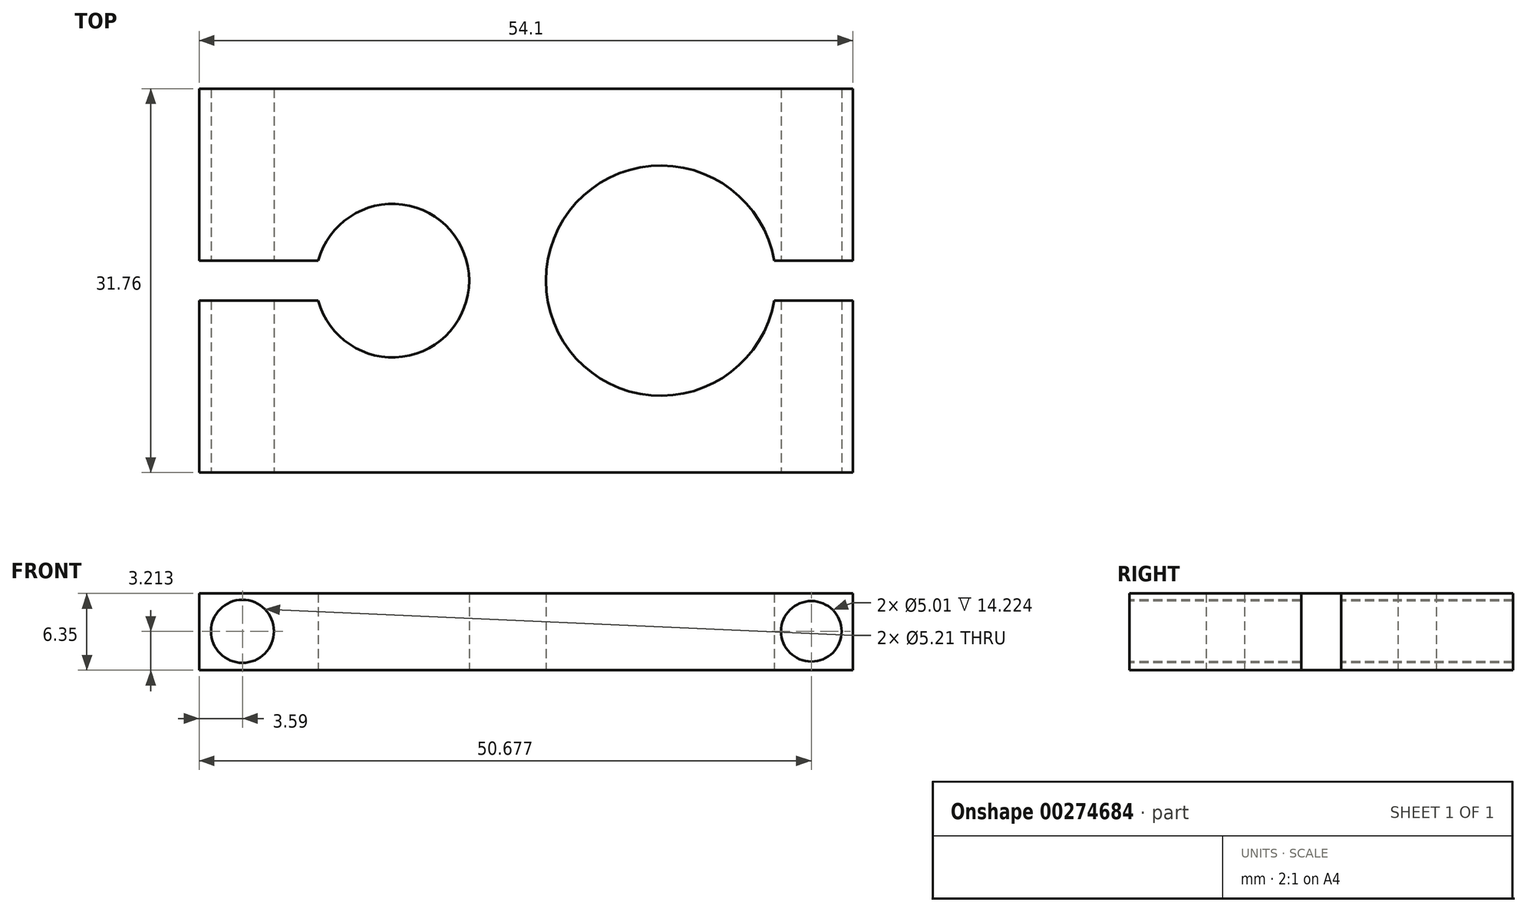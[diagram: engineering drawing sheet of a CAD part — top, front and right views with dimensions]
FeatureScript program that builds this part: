
annotation { "Feature Type Name" : "Feature", "Feature Type Description" : "" }
export const myFeature = defineFeature(function(context is Context, id is Id, definition is map)
    precondition{}
    {
        {
            var Q0;
            Q0=qCreatedBy(makeId("Top.planeOp"),FACE);
            var sketch = newSketch(context, id + "F0", { "sketchPlane" : qUnion([Q0])});
            skLineSegment(sketch, "E0.bottom", {"start": v(-27.05, 15.88) * mm, "end": v(27.05, 15.88) * mm});
            skLineSegment(sketch, "E0.top", {"start": v(-27.05, -15.88) * mm, "end": v(27.05, -15.88) * mm});
            skLineSegment(sketch, "E0.left", {"start": v(-27.05, 15.88) * mm, "end": v(-27.05, 1.65) * mm});
            skLineSegment(sketch, "E0.right", {"start": v(27.05, 15.88) * mm, "end": v(27.05, 1.65) * mm});
            skArc(sketch, "E1", {"start": v(20.56, 1.65) * mm, "mid": v(1.65, 0) * mm, "end": v(20.56, -1.65) * mm});
            skArc(sketch, "E2", {"start": v(-17.18, -1.65) * mm, "mid": v(-4.7, 0) * mm, "end": v(-17.18, 1.65) * mm});
            skLineSegment(sketch, "E3", {"start": v(-27.05, -1.65) * mm, "end": v(-17.18, -1.65) * mm});
            skLineSegment(sketch, "E4", {"start": v(-27.05, 1.65) * mm, "end": v(-17.18, 1.65) * mm});
            skLineSegment(sketch, "E5", {"start": v(20.56, 1.65) * mm, "end": v(27.05, 1.65) * mm});
            skLineSegment(sketch, "E6", {"start": v(27.05, -1.65) * mm, "end": v(20.56, -1.65) * mm});
            skLineSegment(sketch, "E7.trimOffspring", {"start": v(-27.05, -1.65) * mm, "end": v(-27.05, -15.88) * mm});
            skLineSegment(sketch, "E8.trimOffspring", {"start": v(27.05, -1.65) * mm, "end": v(27.05, -15.88) * mm});
            skSolve(sketch);
        }
        {
            var Q0;
            Q0 = qSketchRegion(id + "F0", true);
            var Q1;
            Q1=sQuery(id+"F0.wireOp",EDGE,"E1");
            var Q2;
            Q2=sQuery(id+"F0.wireOp",EDGE,"E0.top");
            var Q3;
            Q3=sQuery(id+"F0.wireOp",EDGE,"E0.right");
            var Q4;
            Q4=sQuery(id+"F0.wireOp",EDGE,"E2");
            var Q5;
            Q5=sQuery(id+"F0.wireOp",EDGE,"E0.left");
            var Q6;
            Q6=sQuery(id+"F0.wireOp",EDGE,"E0.bottom");
            extrude(context, id + "F1", {"entities" : qUnion([Q0]), "surfaceEntities" : qUnion([Q1, Q2, Q3, Q4, Q5, Q6]), "depth" : 6.35 * mm});
        }
        {
            var Q0;
            Q0=makeQuery(id+"F1.opExtrude","SWEPT_FACE",FACE,{"disambiguationData":[OSD([sQuery(id+"F0.wireOp",EDGE,"E0.top")])]});
            var sketch = newSketch(context, id + "F2", { "sketchPlane" : qUnion([Q0])});
            skCircle(sketch, "E9", {"center": v(-23.46, 3.21) * mm, "radius": 2.6 * mm});
            skCircle(sketch, "E10", {"center": v(23.63, 3.21) * mm, "radius": 2.5 * mm});
            skSolve(sketch);
        }
        {
            var Q0;
            Q0 = qSketchRegion(id + "F2", true);
            extrude(context, id + "F3", {"entities" : qUnion([Q0]), "operationType" : NewBodyOperationType.REMOVE, "oppositeDirection" : true, "depth" : 34.3 * mm});
        }
    });
